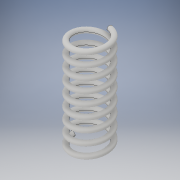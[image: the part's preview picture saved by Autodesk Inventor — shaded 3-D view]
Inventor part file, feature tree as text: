
AUTODESK INVENTOR PART (.ipt)
format: ipt  version: 2018 (Build 220112000, 112)  size: 462,336 bytes
history: native  units: in
note: dims shown in document units (in); Inventor stores cm internally (conversion verified against a paired STEP export)
features: helix x1, sketch x1
ambient origin geometry x8: Origin, YZ Plane, XZ Plane, XY Plane, X Axis, Y Axis, Z Axis, Center Point
bodies: Solid1 (feature_tree)
feature tree (2):
  helix  "Coil1"  [1 undecoded]
  sketch  "Sketch1"  dims[d1=0.0787in d2=1.0in d3=0.374in d4=3.1496in d5=0.0in d6=90.0deg d7=0.2749in d8=90.0deg d9=0.2749in]
note: 1 required parameter value undecoded (feature->parameter linkage not recoverable at this tier; creation-order binding heuristic only, values carry confidence <= 0.55)
